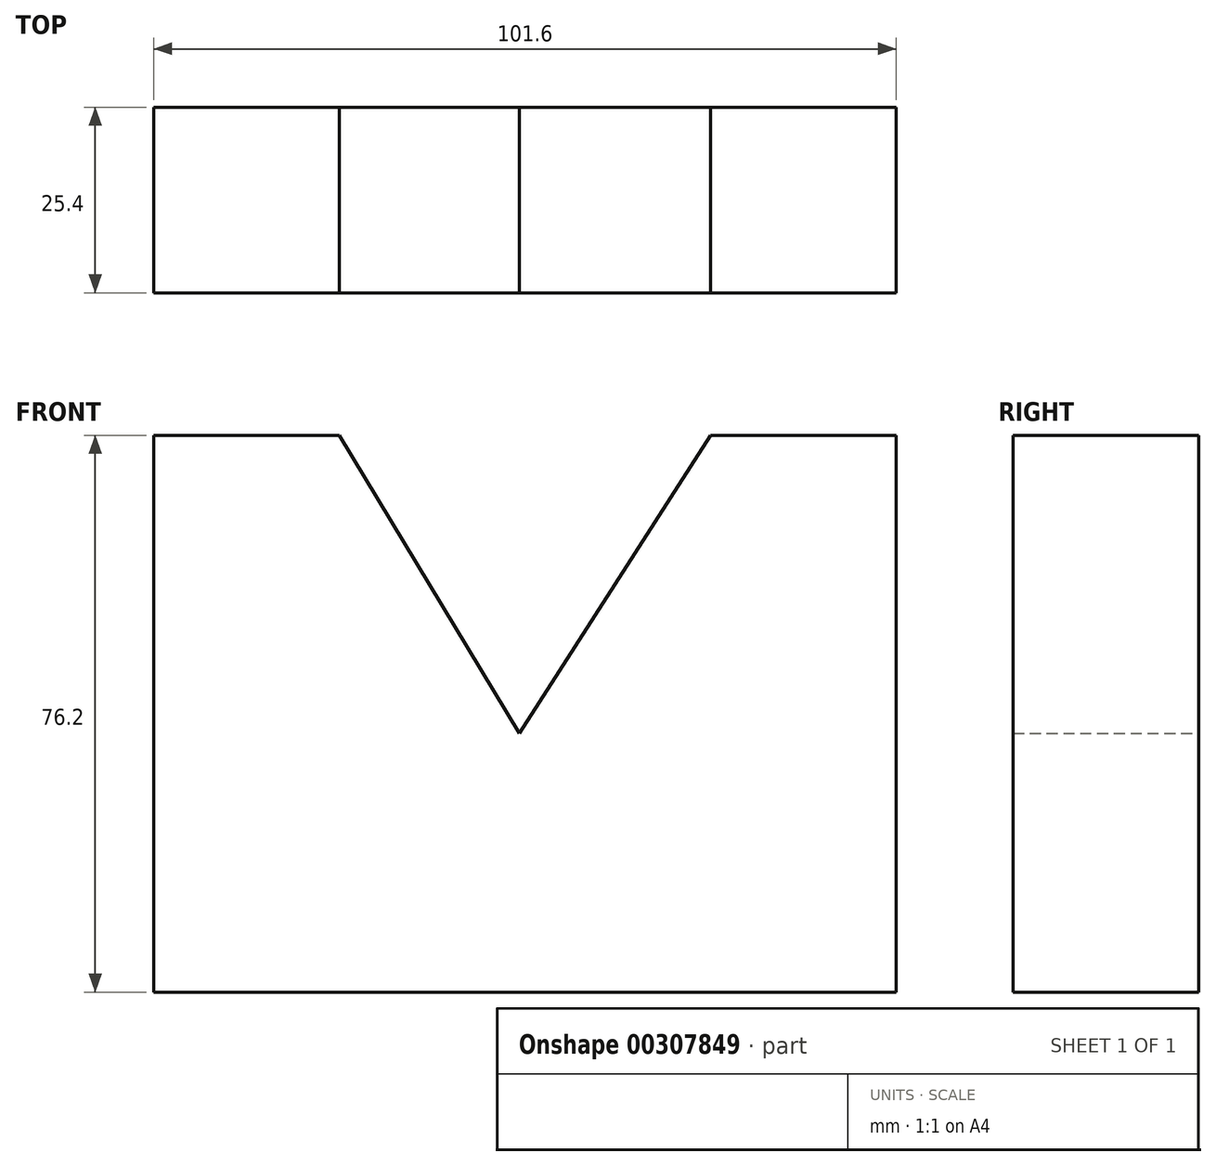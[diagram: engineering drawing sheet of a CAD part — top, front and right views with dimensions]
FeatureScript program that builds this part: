
annotation { "Feature Type Name" : "Feature", "Feature Type Description" : "" }
export const myFeature = defineFeature(function(context is Context, id is Id, definition is map)
    precondition{}
    {
        {
            var Q0;
            Q0=qCreatedBy(makeId("Front.planeOp"),FACE);
            var sketch = newSketch(context, id + "F0", { "sketchPlane" : qUnion([Q0])});
            skLineSegment(sketch, "E0", {"start": v(-34.07, -60.47) * mm, "end": v(67.53, -60.47) * mm});
            skLineSegment(sketch, "E1", {"start": v(67.53, -60.47) * mm, "end": v(67.53, 15.73) * mm});
            skLineSegment(sketch, "E2", {"start": v(67.53, 15.73) * mm, "end": v(42.13, 15.73) * mm});
            skLineSegment(sketch, "E3", {"start": v(42.13, 15.73) * mm, "end": v(16, -25.1) * mm});
            skLineSegment(sketch, "E4", {"start": v(16, -25.1) * mm, "end": v(-8.67, 15.73) * mm});
            skLineSegment(sketch, "E5", {"start": v(-8.67, 15.73) * mm, "end": v(-34.07, 15.73) * mm});
            skLineSegment(sketch, "E6", {"start": v(-34.07, 15.73) * mm, "end": v(-34.07, -60.47) * mm});
            skSolve(sketch);
        }
        {
            var Q0;
            Q0=makeQuery(id+"F0.imprint","IMPRINT",FACE,{"disambiguationData":[TD([[makeQuery(id+"F0.imprint","IMPRINT",EDGE,{"derivedFrom":sQuery(id+"F0.wireOp",EDGE,"E0")}),1.0]])]});
            extrude(context, id + "F1", {"entities" : qUnion([Q0]), "depth" : 25.4 * mm});
        }
    });
